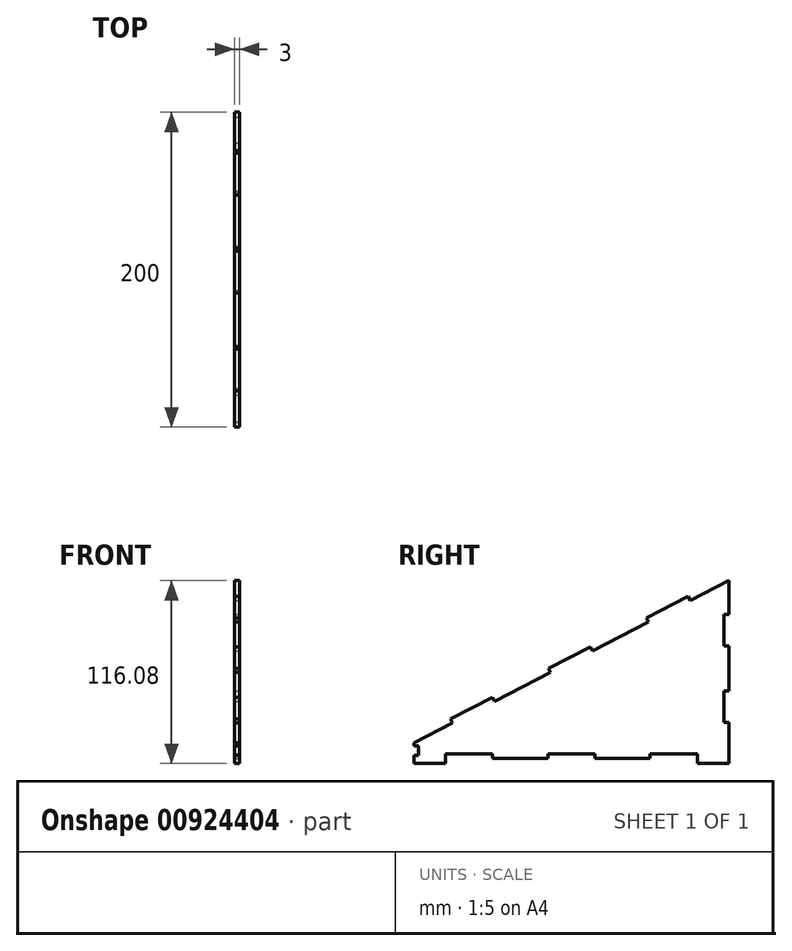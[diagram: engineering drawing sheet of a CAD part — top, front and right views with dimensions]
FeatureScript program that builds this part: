
annotation { "Feature Type Name" : "Feature", "Feature Type Description" : "" }
export const myFeature = defineFeature(function(context is Context, id is Id, definition is map)
    precondition{}
    {
        {
            var Q0;
            Q0=qCreatedBy(makeId("Right.planeOp"),FACE);
            var sketch = newSketch(context, id + "F0", { "sketchPlane" : qUnion([Q0])});
            skLineSegment(sketch, "E0", {"start": v(0, 13) * mm, "end": v(200, 116.08) * mm});
            skLineSegment(sketch, "E1", {"start": v(200, 116.08) * mm, "end": v(200, 13) * mm});
            skLineSegment(sketch, "E2", {"start": v(200, 0) * mm, "end": v(180, 0) * mm});
            skLineSegment(sketch, "E3", {"start": v(180, 0) * mm, "end": v(180, 3) * mm});
            skLineSegment(sketch, "E4", {"start": v(180, 3) * mm, "end": v(20, 3) * mm});
            skLineSegment(sketch, "E5", {"start": v(20, 3) * mm, "end": v(20, 0) * mm});
            skLineSegment(sketch, "E6", {"start": v(20, 0) * mm, "end": v(0, 0) * mm});
            skLineSegment(sketch, "E7", {"start": v(106.67, 67.97) * mm, "end": v(127.74, 27.09) * mm, "construction": true});
            skLineSegment(sketch, "E8", {"start": v(127.74, 27.09) * mm, "end": v(178.4, 53.2) * mm, "construction": true});
            skLineSegment(sketch, "E9", {"start": v(178.4, 53.2) * mm, "end": v(157.33, 94.09) * mm, "construction": true});
            skLineSegment(sketch, "E10", {"start": v(0, 13) * mm, "end": v(0, 0) * mm});
            skLineSegment(sketch, "E11", {"start": v(200, 13) * mm, "end": v(200, 0) * mm});
            skPoint(sketch, "E12.visualSharp", {"position": v(180, 3) * mm});
            skLineSegment(sketch, "E12.filletArc", {"start": v(180, 3) * mm, "end": v(180, 3) * mm});
            skPoint(sketch, "E13.visualSharp", {"position": v(20, 3) * mm});
            skLineSegment(sketch, "E13.filletArc", {"start": v(20, 3) * mm, "end": v(20, 3) * mm});
            skSolve(sketch);
        }
        {
            var Q0;
            Q0=makeQuery(id+"F0.imprint","IMPRINT",FACE,{"disambiguationData":[TD([[makeQuery(id+"F0.imprint","IMPRINT",EDGE,{"derivedFrom":sQuery(id+"F0.wireOp",EDGE,"E0")}),-1.0]])]});
            extrude(context, id + "F1", {"entities" : qUnion([Q0]), "depth" : 3 * mm, "offsetDistance" : 25 * mm});
        }
        {
            var Q0;
            Q0=qCreatedBy(makeId("Right.planeOp"),FACE);
            var sketch = newSketch(context, id + "F2", { "sketchPlane" : qUnion([Q0])});
            skLineSegment(sketch, "E14.bottom", {"start": v(0, 11) * mm, "end": v(3, 11) * mm});
            skLineSegment(sketch, "E14.top", {"start": v(0, 5) * mm, "end": v(3, 5) * mm});
            skLineSegment(sketch, "E14.left", {"start": v(3, 11) * mm, "end": v(3, 5) * mm});
            skLineSegment(sketch, "E14.right", {"start": v(0, 11) * mm, "end": v(0, 5) * mm});
            skSolve(sketch);
        }
        {
            var Q0;
            Q0 = qSketchRegion(id + "F2", true);
            extrude(context, id + "F3", {"entities" : qUnion([Q0]), "operationType" : NewBodyOperationType.REMOVE, "endBound" : BoundingType.THROUGH_ALL, "depth" : 25 * mm, "offsetDistance" : 25 * mm});
        }
        {
            var Q0;
            Q0=makeQuery(id+"F1.opExtrude","CAP_FACE",FACE,{"disambiguationData":[OSD([sQuery(id+"F0.wireOp",EDGE,"E0"),sQuery(id+"F0.wireOp",EDGE,"E1"),sQuery(id+"F0.wireOp",EDGE,"E2"),sQuery(id+"F0.wireOp",EDGE,"E3"),sQuery(id+"F0.wireOp",EDGE,"E4"),sQuery(id+"F0.wireOp",EDGE,"E5"),sQuery(id+"F0.wireOp",EDGE,"E6"),sQuery(id+"F0.wireOp",EDGE,"E10"),sQuery(id+"F0.wireOp",EDGE,"E11")])],"isStart":false});
            var sketch = newSketch(context, id + "F4", { "sketchPlane" : qUnion([Q0])});
            skPoint(sketch, "E15.oppositeSnap0", {"position": v(3, 8) * mm});
            skLineSegment(sketch, "E16.bottom", {"start": v(150, 6) * mm, "end": v(180, 6) * mm});
            skLineSegment(sketch, "E16.top", {"start": v(150, 3) * mm, "end": v(180, 3) * mm});
            skLineSegment(sketch, "E16.left", {"start": v(150, 6) * mm, "end": v(150, 3) * mm});
            skLineSegment(sketch, "E16.right", {"start": v(180, 6) * mm, "end": v(180, 3) * mm});
            skLineSegment(sketch, "E17.bottom", {"start": v(20, 3) * mm, "end": v(50, 3) * mm});
            skLineSegment(sketch, "E17.top", {"start": v(20, 6) * mm, "end": v(50, 6) * mm});
            skLineSegment(sketch, "E17.left", {"start": v(20, 3) * mm, "end": v(20, 6) * mm});
            skLineSegment(sketch, "E17.right", {"start": v(50, 3) * mm, "end": v(50, 6) * mm});
            skLineSegment(sketch, "E18.bottom", {"start": v(85, 3) * mm, "end": v(115, 3) * mm});
            skLineSegment(sketch, "E18.top", {"start": v(85, 6) * mm, "end": v(115, 6) * mm});
            skLineSegment(sketch, "E18.left", {"start": v(85, 3) * mm, "end": v(85, 6) * mm});
            skLineSegment(sketch, "E18.right", {"start": v(115, 3) * mm, "end": v(115, 6) * mm});
            skLineSegment(sketch, "E19", {"start": v(50, 4.5) * mm, "end": v(85, 4.5) * mm, "construction": true});
            skLineSegment(sketch, "E20.bottom", {"start": v(115, 4.5) * mm, "end": v(150, 4.5) * mm});
            skLineSegment(sketch, "E20.top", {"start": v(115, 4.5) * mm, "end": v(150, 4.5) * mm, "construction": true});
            skLineSegment(sketch, "E20.left", {"start": v(115, 4.5) * mm, "end": v(115, 4.5) * mm});
            skLineSegment(sketch, "E20.right", {"start": v(150, 4.5) * mm, "end": v(150, 4.5) * mm});
            skSolve(sketch);
        }
        {
            var Q0;
            Q0 = qSketchRegion(id + "F4", true);
            extrude(context, id + "F5", {"entities" : qUnion([Q0]), "operationType" : NewBodyOperationType.REMOVE, "endBound" : BoundingType.THROUGH_ALL, "oppositeDirection" : true, "depth" : 25 * mm, "offsetDistance" : 25 * mm});
        }
        {
            var Q0;
            Q0=makeQuery(id+"F1.opExtrude","CAP_FACE",FACE,{"disambiguationData":[OSD([sQuery(id+"F0.wireOp",EDGE,"E0"),sQuery(id+"F0.wireOp",EDGE,"E1"),sQuery(id+"F0.wireOp",EDGE,"E2"),sQuery(id+"F0.wireOp",EDGE,"E3"),sQuery(id+"F0.wireOp",EDGE,"E4"),sQuery(id+"F0.wireOp",EDGE,"E5"),sQuery(id+"F0.wireOp",EDGE,"E6"),sQuery(id+"F0.wireOp",EDGE,"E10"),sQuery(id+"F0.wireOp",EDGE,"E11")])],"isStart":false});
            var sketch = newSketch(context, id + "F6", { "sketchPlane" : qUnion([Q0])});
            skLineSegment(sketch, "E21", {"start": v(197, 114.53) * mm, "end": v(197, 0) * mm, "construction": true});
            skLineSegment(sketch, "E22.bottom", {"start": v(200, 26) * mm, "end": v(197, 26) * mm});
            skLineSegment(sketch, "E22.top", {"start": v(200, 46) * mm, "end": v(197, 46) * mm});
            skLineSegment(sketch, "E22.left", {"start": v(200, 26) * mm, "end": v(200, 46) * mm});
            skLineSegment(sketch, "E22.right", {"start": v(197, 26) * mm, "end": v(197, 46) * mm});
            skLineSegment(sketch, "E23.bottom", {"start": v(197, 94.53) * mm, "end": v(200, 94.53) * mm});
            skLineSegment(sketch, "E23.top", {"start": v(197, 74.53) * mm, "end": v(200, 74.53) * mm});
            skLineSegment(sketch, "E23.left", {"start": v(197, 94.53) * mm, "end": v(197, 74.53) * mm});
            skLineSegment(sketch, "E23.right", {"start": v(200, 94.53) * mm, "end": v(200, 74.53) * mm});
            skSolve(sketch);
        }
        {
            var Q0;
            Q0=makeQuery(id+"F6.imprint","IMPRINT",FACE,{"disambiguationData":[TD([[makeQuery(id+"F6.imprint","IMPRINT",EDGE,{"derivedFrom":sQuery(id+"F6.wireOp",EDGE,"E23.bottom")}),-1.0]])]});
            var Q1;
            Q1=makeQuery(id+"F6.imprint","IMPRINT",FACE,{"disambiguationData":[TD([[makeQuery(id+"F6.imprint","IMPRINT",EDGE,{"derivedFrom":sQuery(id+"F6.wireOp",EDGE,"E22.bottom")}),-1.0]])]});
            extrude(context, id + "F7", {"entities" : qUnion([Q0, Q1]), "operationType" : NewBodyOperationType.REMOVE, "endBound" : BoundingType.THROUGH_ALL, "oppositeDirection" : true, "depth" : 25 * mm, "offsetDistance" : 25 * mm});
        }
        {
            var Q0;
            Q0=makeQuery(id+"F1.opExtrude","CAP_FACE",FACE,{"disambiguationData":[OSD([sQuery(id+"F0.wireOp",EDGE,"E0"),sQuery(id+"F0.wireOp",EDGE,"E1"),sQuery(id+"F0.wireOp",EDGE,"E2"),sQuery(id+"F0.wireOp",EDGE,"E3"),sQuery(id+"F0.wireOp",EDGE,"E4"),sQuery(id+"F0.wireOp",EDGE,"E5"),sQuery(id+"F0.wireOp",EDGE,"E6"),sQuery(id+"F0.wireOp",EDGE,"E10"),sQuery(id+"F0.wireOp",EDGE,"E11")])],"isStart":false});
            var sketch = newSketch(context, id + "F8", { "sketchPlane" : qUnion([Q0])});
            skLineSegment(sketch, "E24", {"start": v(0, 13) * mm, "end": v(200, 116.08) * mm, "construction": true});
            skLineSegment(sketch, "E25", {"start": v(24.44, 25.6) * mm, "end": v(23.07, 28.27) * mm});
            skLineSegment(sketch, "E26", {"start": v(23.07, 28.27) * mm, "end": v(49.74, 42) * mm});
            skLineSegment(sketch, "E27", {"start": v(49.74, 42) * mm, "end": v(51.11, 39.34) * mm});
            skLineSegment(sketch, "E28", {"start": v(148.89, 89.74) * mm, "end": v(147.51, 92.4) * mm});
            skLineSegment(sketch, "E29", {"start": v(147.51, 92.4) * mm, "end": v(174.18, 106.15) * mm});
            skLineSegment(sketch, "E30", {"start": v(174.18, 106.15) * mm, "end": v(175.56, 103.48) * mm});
            skLineSegment(sketch, "E31", {"start": v(175.56, 103.48) * mm, "end": v(148.89, 89.74) * mm});
            skLineSegment(sketch, "E32", {"start": v(51.11, 39.34) * mm, "end": v(24.44, 25.6) * mm});
            skLineSegment(sketch, "E33", {"start": v(86.67, 57.67) * mm, "end": v(85.3, 60.33) * mm});
            skLineSegment(sketch, "E34", {"start": v(85.3, 60.33) * mm, "end": v(111.96, 74.08) * mm});
            skLineSegment(sketch, "E35", {"start": v(111.96, 74.08) * mm, "end": v(113.33, 71.41) * mm});
            skLineSegment(sketch, "E36", {"start": v(113.33, 71.41) * mm, "end": v(86.67, 57.67) * mm});
            skPoint(sketch, "E37", {"position": v(100, 64.54) * mm});
            skSolve(sketch);
        }
        {
            var Q0;
            Q0 = qSketchRegion(id + "F8", true);
            var Q1;
            Q1=makeQuery(id+"F1.opExtrude","CAP_FACE",FACE,{"disambiguationData":[OSD([sQuery(id+"F0.wireOp",EDGE,"E0"),sQuery(id+"F0.wireOp",EDGE,"E1"),sQuery(id+"F0.wireOp",EDGE,"E2"),sQuery(id+"F0.wireOp",EDGE,"E3"),sQuery(id+"F0.wireOp",EDGE,"E4"),sQuery(id+"F0.wireOp",EDGE,"E5"),sQuery(id+"F0.wireOp",EDGE,"E6"),sQuery(id+"F0.wireOp",EDGE,"E10"),sQuery(id+"F0.wireOp",EDGE,"E11")])],"isStart":true});
            extrude(context, id + "F9", {"entities" : qUnion([Q0]), "operationType" : NewBodyOperationType.ADD, "endBound" : BoundingType.UP_TO_SURFACE, "oppositeDirection" : true, "depth" : 25 * mm, "endBoundEntityFace" : qUnion([Q1]), "offsetDistance" : 25 * mm});
        }
    });
